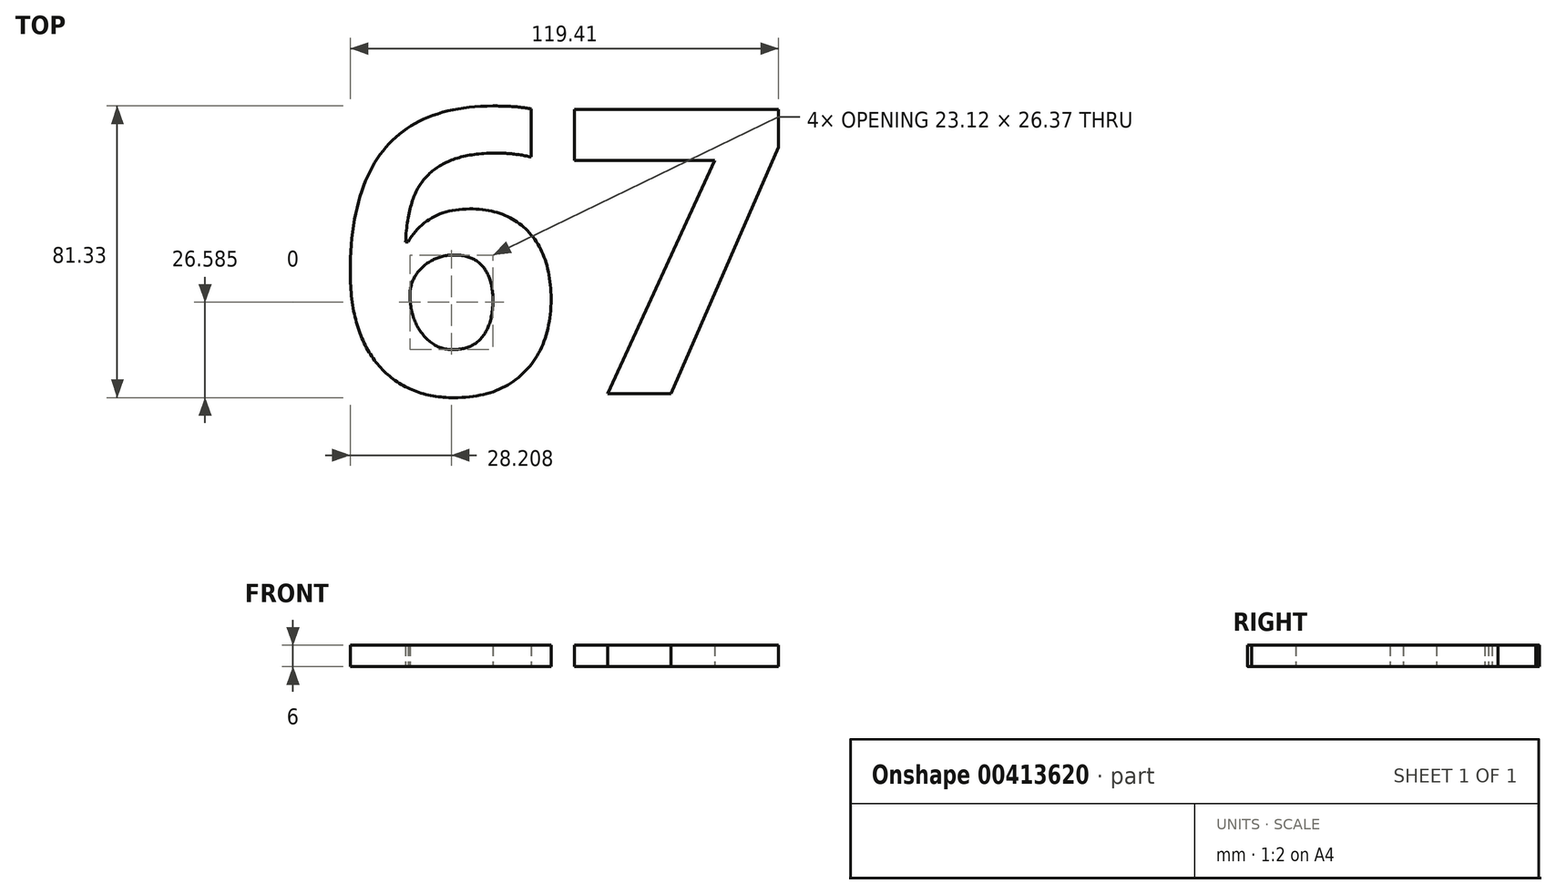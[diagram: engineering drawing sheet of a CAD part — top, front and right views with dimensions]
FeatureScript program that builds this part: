
annotation { "Feature Type Name" : "Feature", "Feature Type Description" : "" }
export const myFeature = defineFeature(function(context is Context, id is Id, definition is map)
    precondition{}
    {
        {
            var Q0;
            Q0=qCreatedBy(makeId("Top.planeOp"),FACE);
            var sketch = newSketch(context, id + "F0", { "sketchPlane" : qUnion([Q0])});
            skText(sketch, "E0", { "text": "67", "fontName": "OpenSans-Bold.ttf"});
            const initialGuessF0  = {"E0": [-0.05275, -0.06, 1, 0, 0.08]};
            skSetInitialGuess(sketch, initialGuessF0);
            skSolve(sketch);
        }
        {
            var Q0;
            Q0=makeQuery(id+"F0.imprint","IMPRINT",FACE,{"disambiguationData":[TD([[makeQuery(id+"F0.imprint","IMPRINT",EDGE,{"derivedFrom":sQuery(id+"F0.wireOp",EDGE,"E0.sketch_text.stroke-0")}),-1.0]])]});
            var Q1;
            Q1=makeQuery(id+"F0.imprint","IMPRINT",FACE,{"disambiguationData":[TD([[makeQuery(id+"F0.imprint","IMPRINT",EDGE,{"derivedFrom":sQuery(id+"F0.wireOp",EDGE,"E0.sketch_text.stroke-25")}),-1.0]])]});
            extrude(context, id + "F1", {"entities" : qUnion([Q0, Q1]), "depth" : 6 * mm, "offsetDistance" : 25 * mm});
        }
    });
